# Revit family: SANINDUSA_108540_Link_LinkCeramicBathroomDivider42x9x75_V0
name_source: partatom
category: Generic Models
units: mm (PartAtom-declared; Revit-internal decimal feet)

## family parameters
Always vertical = Yes
Can host rebar = No
Cut with Voids When Loaded = No
OmniClass Number = 23.45.00.00
OmniClass Title = Sanitary, Laundry, and Cleaning Equipment
Part Type = Normal
Room Calculation Point = No
Round Connector Dimension = Use Diameter
Shared = No
Work Plane-Based = Yes

## types (1)
- SANINDUSA_108540_Link_LinkCeramicBathroomDivider42x9x75_V0
    AssetType = Fixed
    Color = white
    Constituents = 10854010 - Kit de fixação para separador de urinol Link (included).
    Cost = 0 $
    Default Elevation = 1219 mm
    Edition number = 1
    Element Type = bathroom divider
    Features = bathroom divider
    Finish = gloss
    Installation Instructions = https://www.tec.sanindusa.pt
    ManufacturerName = Sanindusa
    ManufacturerURL = www.tec.sanindusa.pt
    Material = Fine Fireclay
    Model = 108540
    ModelNumber = 108540
    ModelReference = Link
    Name = Link ceramic bathroom divider
    NominalHeight = 750 mm  [stored 2.46063 ft]
    NominalLength = 420 mm  [stored 1.37795 ft]
    NominalWidth = 88 mm  [stored 0.288714 ft]
    Pre-defined type (IFC) = FURNISHINGELEMENT
    ProductInformation = https://www.tec.sanindusa.pt
    ProductionYear = 2011
    Size = 42x9x75
    Type (IFC) = IfcFurnitureType
    URL = www.tec.sanindusa.pt
    Uniclass2015Code = Pr_40_20_93_62
    Uniclass2015Title = Pre-plumbedinstallationframes
    Uniclass2015Version = Productsv1.6
    Version = 1
    WarrantyDescription = https://www.tec.sanindusa.pt
    WarrantyDurationParts = 5
    WarrantyDurationUnit = year
    Weight = 14.90 kg

note: [stored X ft] marks values corroborated as IEEE doubles in the binary element streams (Revit-internal decimal feet)

## geometry (parser evidence)
native form markers: Sweep x8
no freeform markers — native parametric forms only
